# Revit family: Domotics-DomesticRanges-GEWISS-CHORUS_SIGNALLING-LAMP_0.5M
name_source: partatom
category: Apparecchi elettrici
revit_build: Autodesk Revit 2016 (Build: 20161004_0715(x64)
units: mm (PartAtom-declared; Revit-internal decimal feet)

## family parameters
Condiviso = Sì
Host = Superficie
Mantenere orientamento annotazione = Sì
Punto di calcolo locali = Sì
Quota connettore circolare = Usa diametro
Taglio con vuoti quando caricato = Sì
Tipo di parte = Normale

## types (12) — shared parameters
Catalogue = DOMOTICS
Catalogue Range = CHORUS - DOMESTIC RANGE
Description. = Flat indicator lamp
Electrocod = 0132
IDF = fd2b0701-367a-40c7-be54-6d495f8c46b7
IDT = cfaedf2c-0fc5-4d9f-b78a-c0dc01b3f608
Immagine tipo = GW14644.jpg
No. Chorus modules = 1/2
Produttore = GEWISS S.p.A.
Prospetto di default = 1219 mm
SEO = Indicator
Signalling unit = With wired lead
Technical sheet = https://www.gewiss.com
Tipo_ = Chorus Spie 05M_GENERICO : GW14644 Spia di segnalazione ambra 1/2M titanio
URL = https://www.gewiss.com
Version file RFA = 19.0

## per-type parameters (varying)
| type | Colour | Colour meaning | Descrizione | Diffuser colour | EAN code | Modello |
| GW10642 - Green indicator lamp 1/2M white | White | Safety | GREEN INDICATOR LAMP 1/2M WHITE | Green | 8011564259775 | GW10642 |
| GW14643 - Red indicator lamp 1/2M titanium | Titanium | Danger | RED INDICATOR LAMP 1/2M TITANIUM | Red | 8011564268623 | GW14643 |
| GW12644 - Amber indicator lamp 1/2M black | Black | Attention | AMBER INDICATOR LAMP 1/2M BLACK | Amber | 8011564266810 | GW12644 |
| GW10643 - Red indicator lamp 1/2M white | White | Danger | RED INDICATOR LAMP 1/2M WHITE | Red | 8011564259782 | GW10643 |
| GW14641 - Transparent indicator lamp 1/2M titanium | Titanium | Neutral | TRANSPARENT INDICATOR LAMP 1/2M TITANIUM | Opal | 8011564268609 | GW14641 |
| GW10644 - Amber indicator lamp 1/2M white | White | Attention | AMBER INDICATOR LAMP 1/2M WHITE | Amber | 8011564259799 | GW10644 |
| GW10641 - Transparent indicator lamp 1/2M white | White | Neutral | TRANSPARENT INDICATOR LAMP 1/2M WHITE | Opal | 8011564259768 | GW10641 |
| GW14644 - Amber indicator lamp 1/2M titanium | Titanium | Attention | AMBER INDICATOR LAMP 1/2M TITANIUM | Amber | 8011564268630 | GW14644 |
| GW12642 - Green indicator lamp 1/2M black | Black | Safety | GREEN INDICATOR LAMP 1/2M BLACK | Green | 8011564266698 | GW12642 |
| GW14642 - Green indicator lamp 1/2M titanium | Titanium | Safety | GREEN INDICATOR LAMP 1/2M TITANIUM | Green | 8011564268616 | GW14642 |
| GW12643 - Red indicator lamp 1/2M black | Black | Danger | RED INDICATOR LAMP 1/2M BLACK | Red | 8011564266704 | GW12643 |
| GW12641 - Transparent indicator lamp 1/2M black | Black | Neutral | TRANSPARENT INDICATOR LAMP 1/2M BLACK | Opal | 8011564266681 | GW12641 |

## geometry (parser evidence)
native form markers: Sweep x1
no freeform markers — native parametric forms only
